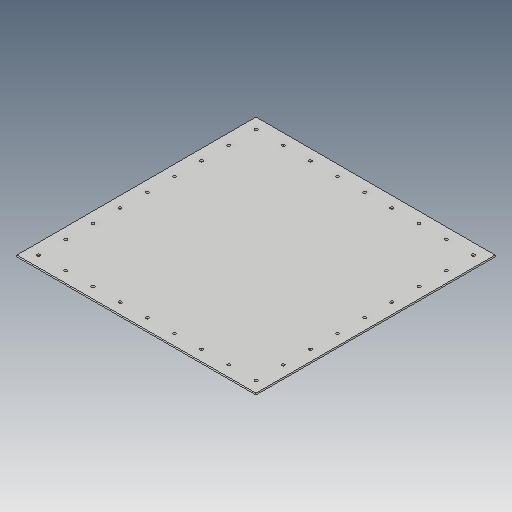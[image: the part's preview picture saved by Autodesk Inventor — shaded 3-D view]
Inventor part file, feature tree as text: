
AUTODESK INVENTOR PART (.ipt)
format: ipt  version: 2017 (Build 210142000, 142)  size: 143,872 bytes
history: native  units: in
note: dims shown in document units (in); Inventor stores cm internally (conversion verified against a paired STEP export)
features: extrude x2, sketch x2
ambient origin geometry x8: Origin, YZ Plane, XZ Plane, XY Plane, X Axis, Y Axis, Z Axis, Center Point
bodies: Body1 (feature_tree)
feature tree (4):
  extrude  "panel body"  Depth=17.3228in
  extrude  "Extrusion4"  Depth=0.3937in
  sketch  "Sketch1"  dims[d0=17.3228in d1=17.3228in]
  sketch  "Sketch2"  dims[d159=0.1181in d160=0.0in d161=15.748in d162=15.748in d163=0.2165in d178=1.0in d179=0.0in d208=3.5433in d210=1.9685in d211=0.3937in d213=1.0in d215=3.5433in d217=1.9685in d218=0.3937in d220=1.0in d222=3.5433in d224=1.9685in d225=0.3937in d227=1.0in d229=3.1496in d231=1.9685in d232=0.3937in d234=1.0in]
